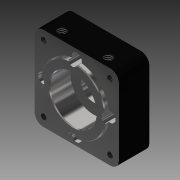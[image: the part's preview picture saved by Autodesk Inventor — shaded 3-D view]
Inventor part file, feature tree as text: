
AUTODESK INVENTOR PART (.ipt)
format: ipt  version: 2013 (Build 170138000, 138)  size: 237,568 bytes
history: native  units: in
note: dims shown in document units (in); Inventor stores cm internally (conversion verified against a paired STEP export)
features: thread x8, extrude x5, sketch x3, fillet x1, chamfer x1
ambient origin geometry x8: Origin, YZ Plane, XZ Plane, XY Plane, X Axis, Y Axis, Z Axis, Center Point
bodies: Solid1 (feature_tree)
feature tree (18):
  sketch  "Sketch1"  dims[d0=0.75in d2=2.5in]
  extrude  "Extrusion1"  Depth=2.5in
  extrude  "Extrusion2"  Depth=0.185in
  extrude  "Extrusion3"  Depth=1.0in
  fillet  "Fillet1"  Radius=1.0in
  chamfer  "Chamfer1"  Distance=1.0in
  thread  "Thread1"  [1 undecoded]
  thread  "Thread2"  [1 undecoded]
  thread  "Thread3"  [1 undecoded]
  thread  "Thread4"  [1 undecoded]
  extrude  "Extrusion4"  Depth=0.1575in
  extrude  "Extrusion5"  Depth=0.97in
  thread  "Thread5"  [1 undecoded]
  thread  "Thread6"  [1 undecoded]
  thread  "Thread7"  [1 undecoded]
  thread  "Thread8"  [1 undecoded]
  sketch  "Sketch2"  dims[d3=2.5in d4=0.185in]
  sketch  "Sketch3"  dims[d5=1.94in d6=1.0in d7=1.0in d8=1.0in d9=1.0in d10=1.375in d11=0.902in d12=0.0in d13=2.125in d14=2.125in d15=0.1575in d16=0.97in d17=0.3in d18=0.5in d19=0.0in d20=0.1181in d21=0.0in d22=0.25in d23=0.025in d24=0.125in d25=45.0deg d26=0.167in d27=1.0in d28=0.0in d29=1.0in d30=0.0in d31=1.0in d32=0.0in d33=1.0in d34=0.0in d35=1.378in d37=0.25in d38=0.652in d39=0.5in d40=0.0in d41=0.25in d43=0.652in d44=1.378in d45=0.5in d46=0.0in d47=1.0in d48=0.0in d49=1.0in d50=0.0in d51=1.0in d52=0.0in d53=1.0in d54=0.0in]
note: 8 required parameter values undecoded (feature->parameter linkage not recoverable at this tier; creation-order binding heuristic only, values carry confidence <= 0.55)
